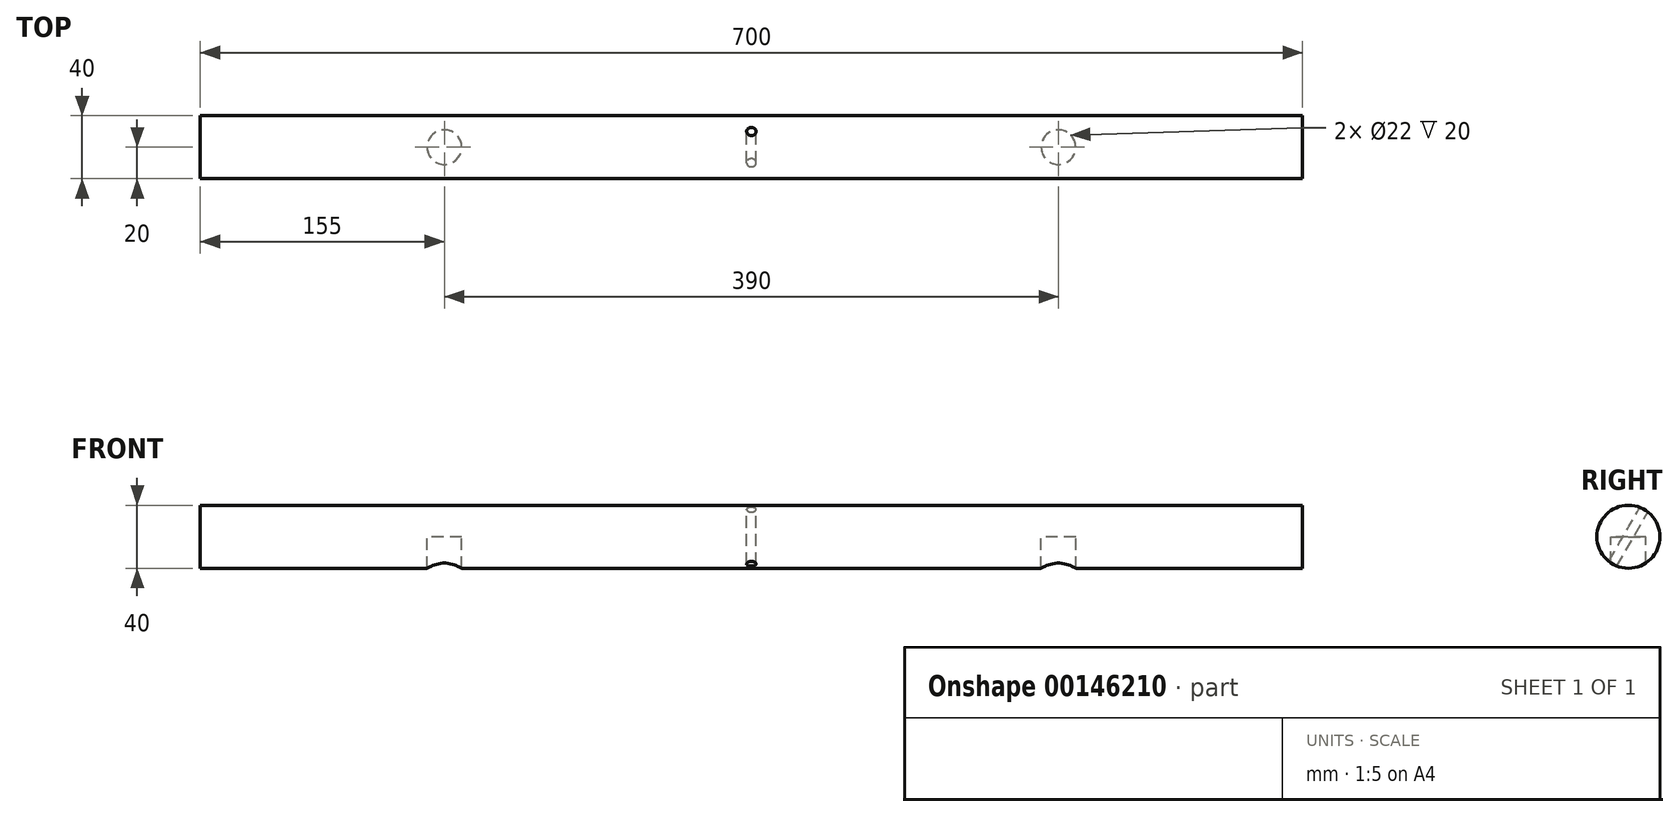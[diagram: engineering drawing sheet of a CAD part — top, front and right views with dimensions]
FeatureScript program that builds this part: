
annotation { "Feature Type Name" : "Feature", "Feature Type Description" : "" }
export const myFeature = defineFeature(function(context is Context, id is Id, definition is map)
    precondition{}
    {
        {
            var Q0;
            Q0=qCreatedBy(makeId("Right.planeOp"),FACE);
            var sketch = newSketch(context, id + "F0", { "sketchPlane" : qUnion([Q0])});
            skCircle(sketch, "E0", {"center": v(0, 0) * mm, "radius": 20 * mm});
            skLineSegment(sketch, "E1", {"start": v(0, 0) * mm, "end": v(10, 17.32) * mm});
            skLineSegment(sketch, "E2", {"start": v(1.34, 22.32) * mm, "end": v(18.66, 12.32) * mm});
            skSolve(sketch);
        }
        {
            var Q0;
            Q0 = qSketchRegion(id + "F0", true);
            extrude(context, id + "F1", {"entities" : qUnion([Q0]), "depth" : 700 * mm, "symmetric" : true});
        }
        {
            var Q0;
            Q0=qCreatedBy(makeId("Top.planeOp"),FACE);
            var sketch = newSketch(context, id + "F2", { "sketchPlane" : qUnion([Q0])});
            skCircle(sketch, "E3", {"center": v(-195, 0) * mm, "radius": 11 * mm});
            skCircle(sketch, "E4.MirrorC", {"center": v(195, 0) * mm, "radius": 11 * mm});
            skSolve(sketch);
        }
        {
            var Q0;
            Q0 = qSketchRegion(id + "F2", true);
            extrude(context, id + "F3", {"entities" : qUnion([Q0]), "operationType" : NewBodyOperationType.REMOVE, "oppositeDirection" : true, "depth" : 25.4 * mm});
        }
        {
            var Q0;
            Q0=sQuery(id+"F0.wireOp",EDGE,"E2");
            var Q1;
            Q1=makeQuery(id+"F1.opExtrude","SWEPT_FACE",FACE,{"disambiguationData":[OSD([sQuery(id+"F0.wireOp",EDGE,"E0")])]});
            cPlane(context, id + "F4", {"entities" : qUnion([Q0, Q1]), "cplaneType" : CPlaneType.LINE_ANGLE, "offset" : 25.4 * mm, "angle" : 0 * degree, "width" : 152.4 * mm, "height" : 152.4 * mm});
        }
        {
            var Q0;
            Q0=qCreatedBy(id+"F4.planeOp",FACE);
            var sketch = newSketch(context, id + "F5", { "sketchPlane" : qUnion([Q0])});
            skCircle(sketch, "E5", {"center": v(0, 0) * mm, "radius": 3 * mm});
            skSolve(sketch);
        }
        {
            var Q0;
            Q0 = qSketchRegion(id + "F5", true);
            extrude(context, id + "F6", {"entities" : qUnion([Q0]), "operationType" : NewBodyOperationType.REMOVE, "endBound" : BoundingType.THROUGH_ALL, "oppositeDirection" : true, "depth" : 25.4 * mm});
        }
    });
